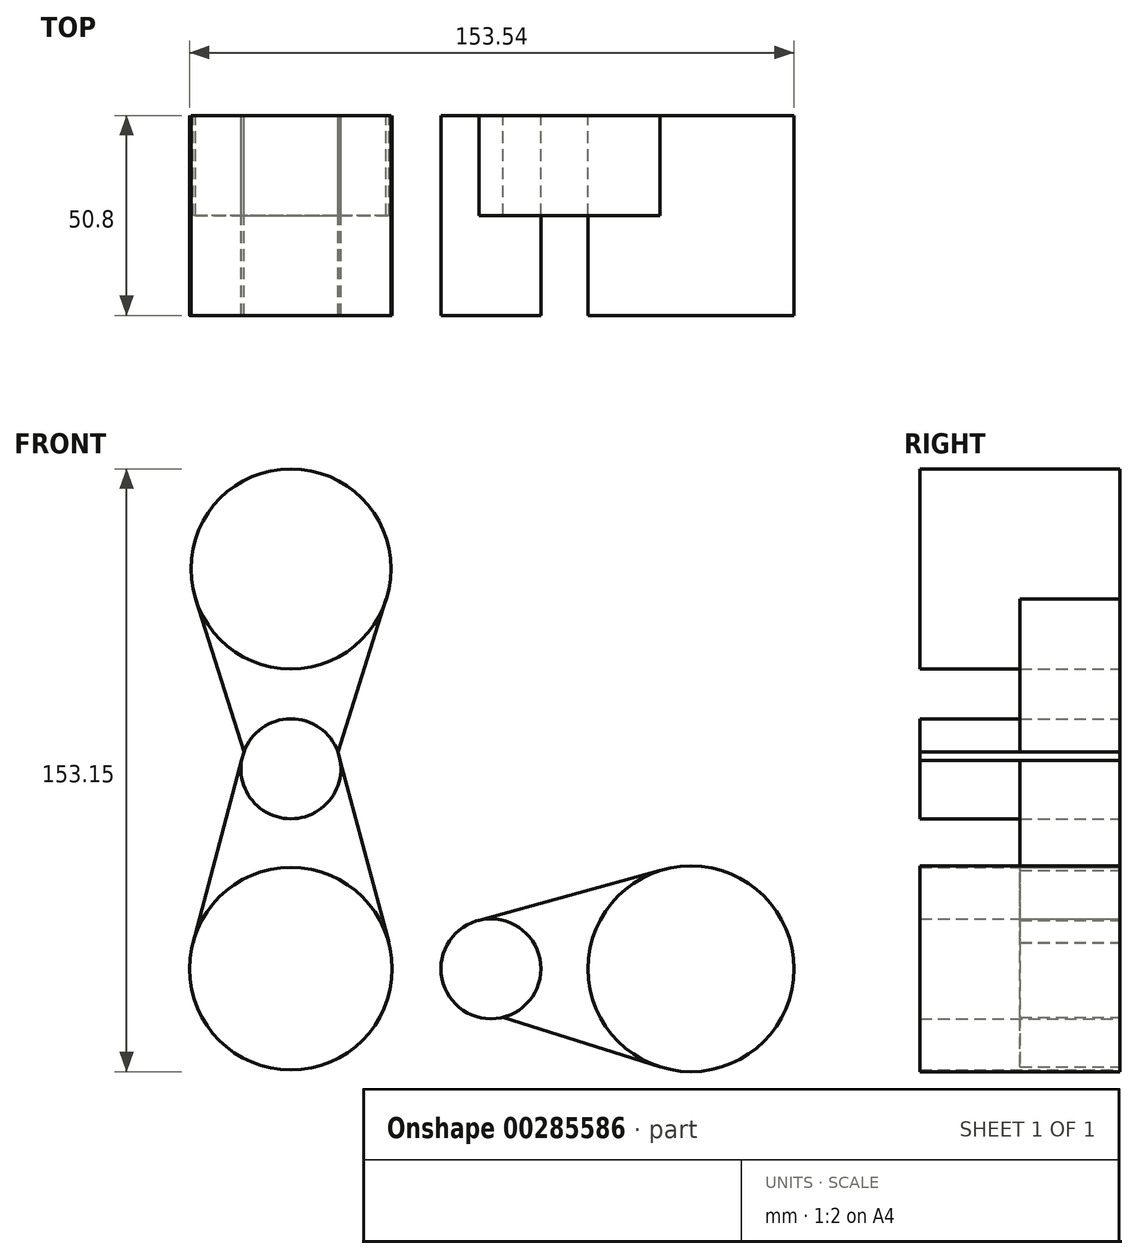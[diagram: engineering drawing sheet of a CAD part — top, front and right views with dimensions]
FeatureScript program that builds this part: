
annotation { "Feature Type Name" : "Feature", "Feature Type Description" : "" }
export const myFeature = defineFeature(function(context is Context, id is Id, definition is map)
    precondition{}
    {
        {
            var Q0;
            Q0=qCreatedBy(makeId("Front.planeOp"),FACE);
            var sketch = newSketch(context, id + "F0", { "sketchPlane" : qUnion([Q0])});
            skLineSegment(sketch, "E0", {"start": v(-143.84, -79.83) * mm, "end": v(-93.04, -79.83) * mm});
            skLineSegment(sketch, "E1", {"start": v(-93.04, -79.83) * mm, "end": v(-42.2, -79.83) * mm});
            skLineSegment(sketch, "E2", {"start": v(-143.84, -79.83) * mm, "end": v(-143.84, -29.03) * mm});
            skLineSegment(sketch, "E3", {"start": v(-143.84, -29.03) * mm, "end": v(-143.84, 21.77) * mm});
            skCircle(sketch, "E4", {"center": v(-143.84, 21.77) * mm, "radius": 25.4 * mm});
            skCircle(sketch, "E5", {"center": v(-143.84, -79.83) * mm, "radius": 25.74 * mm});
            skCircle(sketch, "E6", {"center": v(-42.2, -79.83) * mm, "radius": 26.16 * mm});
            skCircle(sketch, "E7", {"center": v(-143.84, -29.03) * mm, "radius": 12.7 * mm});
            skCircle(sketch, "E8", {"center": v(-93.04, -79.83) * mm, "radius": 12.7 * mm});
            skLineSegment(sketch, "E9", {"start": v(-168.06, 14.14) * mm, "end": v(-155.8, -24.77) * mm});
            skLineSegment(sketch, "E10", {"start": v(-155.8, -24.77) * mm, "end": v(-168.7, -73.2) * mm});
            skLineSegment(sketch, "E11", {"start": v(-119.62, 14.1) * mm, "end": v(-131.9, -24.7) * mm});
            skLineSegment(sketch, "E12", {"start": v(-131.9, -24.7) * mm, "end": v(-118.96, -73.2) * mm});
            skLineSegment(sketch, "E13", {"start": v(-118.96, -73.2) * mm, "end": v(-96.1, -67.5) * mm});
            skLineSegment(sketch, "E14", {"start": v(-96.1, -67.5) * mm, "end": v(-50.1, -54.9) * mm});
            skLineSegment(sketch, "E15", {"start": v(-50.1, -104.76) * mm, "end": v(-89.92, -92.14) * mm});
            skLineSegment(sketch, "E16", {"start": v(-89.92, -92.14) * mm, "end": v(-132.35, -102.87) * mm});
            skSolve(sketch);
        }
        {
            var Q0;
            {var subQ0=sQuery(id+"F0.wireOp",EDGE,"E4");var subQ1=makeQuery(id+"F0.imprint","INTERSECT",VERTEX,{"derivedFrom":[subQ0,sQuery(id+"F0.wireOp",EDGE,"E9")]});Q0=makeQuery(id+"F0.imprint","IMPRINT",FACE,{"disambiguationData":[TD([[makeQuery(id+"F0.imprint","IMPRINT",EDGE,{"disambiguationData":[TD([[subQ1,-1.0]])],"derivedFrom":subQ0}),1.0]])]});}
            var Q1;
            {var subQ3=sQuery(id+"F0.wireOp",EDGE,"E2");var subQ5=sQuery(id+"F0.wireOp",EDGE,"E3");var subQ6=makeQuery(id+"F0.imprint","INTERSECT",VERTEX,{"derivedFrom":[subQ3,subQ5]});Q1=makeQuery(id+"F0.imprint","IMPRINT",FACE,{"disambiguationData":[TD([[makeQuery(id+"F0.imprint","IMPRINT",EDGE,{"disambiguationData":[TD([[subQ6,1.0]])],"derivedFrom":subQ3}),-1.0]])]});}
            var Q2;
            {var subQ3=sQuery(id+"F0.wireOp",EDGE,"E2");var subQ6=sQuery(id+"F0.wireOp",EDGE,"E3");var subQ8=makeQuery(id+"F0.imprint","INTERSECT",VERTEX,{"derivedFrom":[subQ3,subQ6]});Q2=makeQuery(id+"F0.imprint","IMPRINT",FACE,{"disambiguationData":[TD([[makeQuery(id+"F0.imprint","IMPRINT",EDGE,{"disambiguationData":[TD([[subQ8,1.0]])],"derivedFrom":subQ3}),1.0]])]});}
            var Q3;
            {var subQ0=sQuery(id+"F0.wireOp",EDGE,"E1");var subQ1=sQuery(id+"F0.wireOp",EDGE,"E0");var subQ2=makeQuery(id+"F0.imprint","INTERSECT",VERTEX,{"derivedFrom":[subQ1,subQ0]});Q3=makeQuery(id+"F0.imprint","IMPRINT",FACE,{"disambiguationData":[TD([[makeQuery(id+"F0.imprint","IMPRINT",EDGE,{"disambiguationData":[TD([[subQ2,1.0]])],"derivedFrom":subQ1}),-1.0]])]});}
            var Q4;
            {var subQ0=sQuery(id+"F0.wireOp",EDGE,"E1");var subQ1=sQuery(id+"F0.wireOp",EDGE,"E0");var subQ2=makeQuery(id+"F0.imprint","INTERSECT",VERTEX,{"derivedFrom":[subQ1,subQ0]});Q4=makeQuery(id+"F0.imprint","IMPRINT",FACE,{"disambiguationData":[TD([[makeQuery(id+"F0.imprint","IMPRINT",EDGE,{"disambiguationData":[TD([[subQ2,1.0]])],"derivedFrom":subQ1}),1.0]])]});}
            var Q5;
            {var subQ0=sQuery(id+"F0.wireOp",EDGE,"E6");var subQ1=makeQuery(id+"F0.imprint","INTERSECT",VERTEX,{"derivedFrom":[subQ0,sQuery(id+"F0.wireOp",EDGE,"E14")]});Q5=makeQuery(id+"F0.imprint","IMPRINT",FACE,{"disambiguationData":[TD([[makeQuery(id+"F0.imprint","IMPRINT",EDGE,{"disambiguationData":[TD([[subQ1,-1.0]])],"derivedFrom":subQ0}),1.0]])]});}
            var Q6;
            {var subQ3=sQuery(id+"F0.wireOp",EDGE,"E2");var subQ4=sQuery(id+"F0.wireOp",EDGE,"E0");var subQ5=makeQuery(id+"F0.imprint","INTERSECT",VERTEX,{"derivedFrom":[subQ4,subQ3]});Q6=makeQuery(id+"F0.imprint","IMPRINT",FACE,{"disambiguationData":[TD([[makeQuery(id+"F0.imprint","IMPRINT",EDGE,{"disambiguationData":[TD([[subQ5,-1.0]])],"derivedFrom":subQ4}),-1.0]])]});}
            var Q7;
            {var subQ0=sQuery(id+"F0.wireOp",EDGE,"E2");var subQ1=sQuery(id+"F0.wireOp",EDGE,"E0");var subQ2=makeQuery(id+"F0.imprint","INTERSECT",VERTEX,{"derivedFrom":[subQ1,subQ0]});Q7=makeQuery(id+"F0.imprint","IMPRINT",FACE,{"disambiguationData":[TD([[makeQuery(id+"F0.imprint","IMPRINT",EDGE,{"disambiguationData":[TD([[subQ2,-1.0]])],"derivedFrom":subQ1}),1.0]])]});}
            extrude(context, id + "F1", {"entities" : qUnion([Q0, Q1, Q2, Q3, Q4, Q5, Q6, Q7]), "depth" : 50.8 * mm});
        }
        {
            var Q0;
            {var subQ5=sQuery(id+"F0.wireOp",EDGE,"E9");Q0=makeQuery(id+"F0.imprint","IMPRINT",FACE,{"disambiguationData":[TD([[makeQuery(id+"F0.imprint","IMPRINT",EDGE,{"derivedFrom":subQ5}),1.0]])]});}
            var Q1;
            {var subQ5=sQuery(id+"F0.wireOp",EDGE,"E11");Q1=makeQuery(id+"F0.imprint","IMPRINT",FACE,{"disambiguationData":[TD([[makeQuery(id+"F0.imprint","IMPRINT",EDGE,{"derivedFrom":subQ5}),-1.0]])]});}
            var Q2;
            {var subQ0=sQuery(id+"F0.wireOp",EDGE,"E5");var subQ1=sQuery(id+"F0.wireOp",EDGE,"E2");var subQ2=makeQuery(id+"F0.imprint","INTERSECT",VERTEX,{"derivedFrom":[subQ1,subQ0]});Q2=makeQuery(id+"F0.imprint","IMPRINT",FACE,{"disambiguationData":[TD([[makeQuery(id+"F0.imprint","IMPRINT",EDGE,{"disambiguationData":[TD([[subQ2,-1.0]])],"derivedFrom":subQ1}),1.0]])]});}
            var Q3;
            {var subQ0=sQuery(id+"F0.wireOp",EDGE,"E5");var subQ1=sQuery(id+"F0.wireOp",EDGE,"E2");var subQ2=makeQuery(id+"F0.imprint","INTERSECT",VERTEX,{"derivedFrom":[subQ1,subQ0]});Q3=makeQuery(id+"F0.imprint","IMPRINT",FACE,{"disambiguationData":[TD([[makeQuery(id+"F0.imprint","IMPRINT",EDGE,{"disambiguationData":[TD([[subQ2,-1.0]])],"derivedFrom":subQ1}),-1.0]])]});}
            var Q4;
            {var subQ5=sQuery(id+"F0.wireOp",EDGE,"E14");Q4=makeQuery(id+"F0.imprint","IMPRINT",FACE,{"disambiguationData":[TD([[makeQuery(id+"F0.imprint","IMPRINT",EDGE,{"derivedFrom":subQ5}),-1.0]])]});}
            var Q5;
            {var subQ5=sQuery(id+"F0.wireOp",EDGE,"E15");Q5=makeQuery(id+"F0.imprint","IMPRINT",FACE,{"disambiguationData":[TD([[makeQuery(id+"F0.imprint","IMPRINT",EDGE,{"derivedFrom":subQ5}),-1.0]])]});}
            extrude(context, id + "F2", {"entities" : qUnion([Q0, Q1, Q2, Q3, Q4, Q5]), "depth" : 25.4 * mm});
        }
    });
